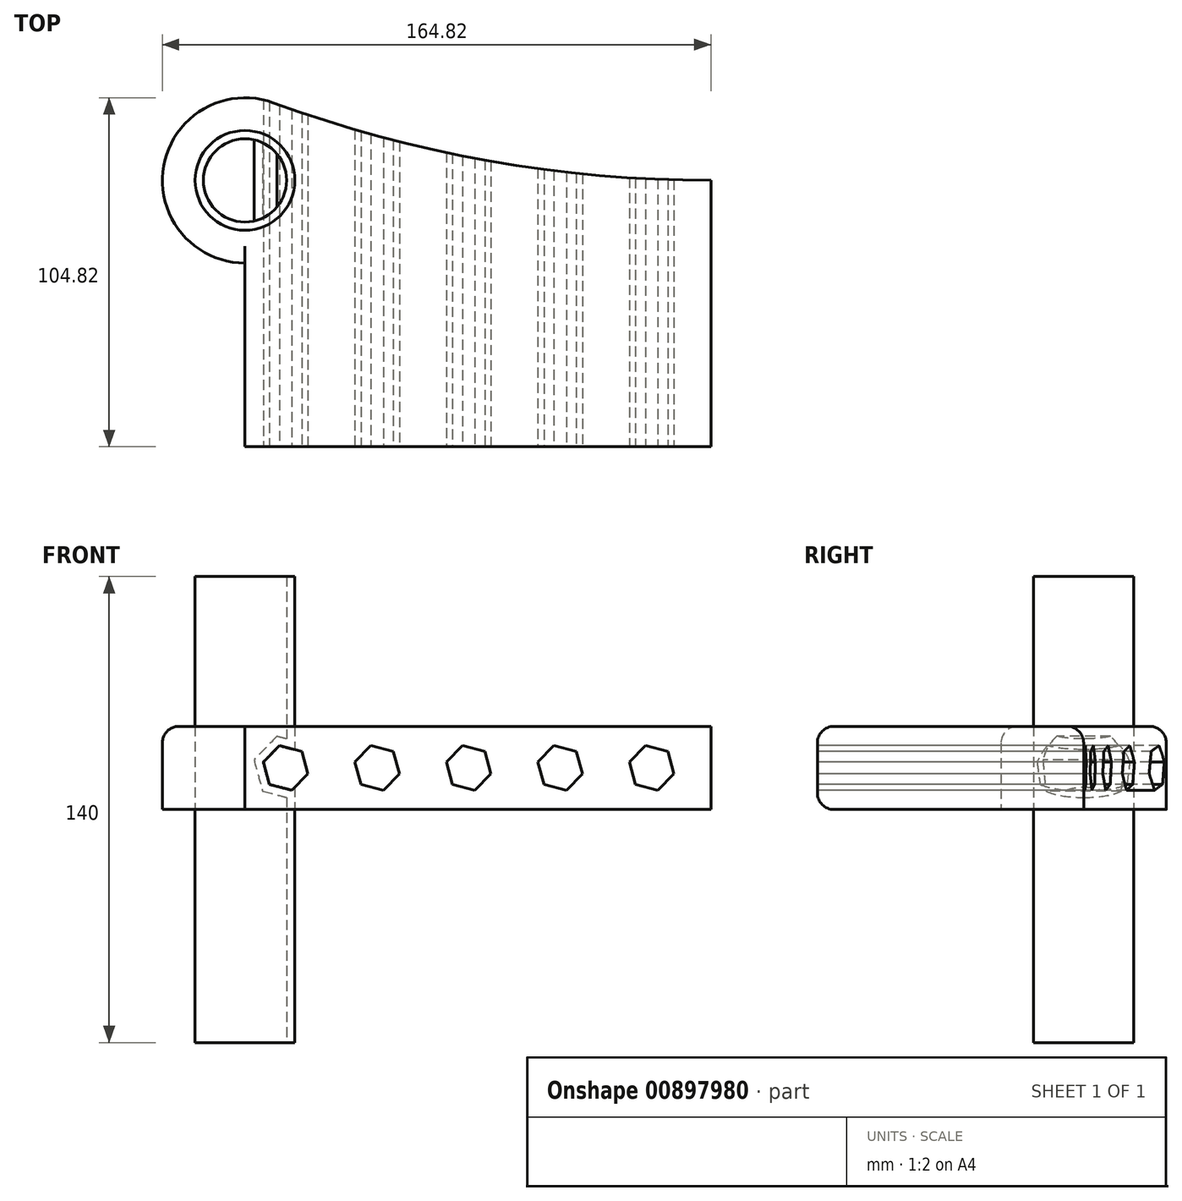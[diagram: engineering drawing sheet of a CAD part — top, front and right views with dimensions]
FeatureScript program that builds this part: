
annotation { "Feature Type Name" : "Feature", "Feature Type Description" : "" }
export const myFeature = defineFeature(function(context is Context, id is Id, definition is map)
    precondition{}
    {
        {
            var Q0;
            Q0=qCreatedBy(makeId("Top.planeOp"),FACE);
            var sketch = newSketch(context, id + "F0", { "sketchPlane" : qUnion([Q0])});
            skLineSegment(sketch, "E0.bottom", {"start": v(70, -40) * mm, "end": v(-70, -40) * mm});
            skLineSegment(sketch, "E0.top", {"start": v(70, 40) * mm, "end": v(-70, 40) * mm});
            skLineSegment(sketch, "E0.left", {"start": v(70, -40) * mm, "end": v(70, 40) * mm});
            skLineSegment(sketch, "E0.right", {"start": v(-70, -40) * mm, "end": v(-70, 40) * mm});
            skPoint(sketch, "E0.middle", {"position": v(0, 0) * mm});
            skCircle(sketch, "E1", {"center": v(-70, 40) * mm, "radius": 24.82 * mm});
            skArc(sketch, "E2", {"start": v(-61.47, 63.3) * mm, "mid": v(3.24, 45.87) * mm, "end": v(70, 40) * mm});
            skCircle(sketch, "E3", {"center": v(-70, 40) * mm, "radius": 15 * mm});
            skSolve(sketch);
        }
        {
            var Q0;
            {var subQ5=sQuery(id+"F0.wireOp",EDGE,"E0.bottom");Q0=makeQuery(id+"F0.imprint","IMPRINT",FACE,{"disambiguationData":[TD([[makeQuery(id+"F0.imprint","IMPRINT",EDGE,{"derivedFrom":subQ5}),-1.0]])]});}
            var Q1;
            {var subQ0=sQuery(id+"F0.wireOp",EDGE,"E1");var subQ4=sQuery(id+"F0.wireOp",EDGE,"E0.top");var subQ5=makeQuery(id+"F0.imprint","INTERSECT",VERTEX,{"derivedFrom":[subQ4,subQ0]});Q1=makeQuery(id+"F0.imprint","IMPRINT",FACE,{"disambiguationData":[TD([[makeQuery(id+"F0.imprint","IMPRINT",EDGE,{"disambiguationData":[TD([[subQ5,-1.0]])],"derivedFrom":subQ4}),-1.0]])]});}
            var Q2;
            {var subQ0=sQuery(id+"F0.wireOp",EDGE,"E2");Q2=makeQuery(id+"F0.imprint","IMPRINT",FACE,{"disambiguationData":[TD([[makeQuery(id+"F0.imprint","IMPRINT",EDGE,{"derivedFrom":subQ0}),-1.0]])]});}
            var Q3;
            {var subQ0=sQuery(id+"F0.wireOp",EDGE,"E1");var subQ1=sQuery(id+"F0.wireOp",EDGE,"E0.top");var subQ2=makeQuery(id+"F0.imprint","INTERSECT",VERTEX,{"derivedFrom":[subQ1,subQ0]});Q3=makeQuery(id+"F0.imprint","IMPRINT",FACE,{"disambiguationData":[TD([[makeQuery(id+"F0.imprint","IMPRINT",EDGE,{"disambiguationData":[TD([[subQ2,-1.0]])],"derivedFrom":subQ1}),1.0]])]});}
            extrude(context, id + "F1", {"entities" : qUnion([Q0, Q1, Q2, Q3]), "depth" : 25 * mm, "offsetDistance" : 25 * mm});
        }
        {
            var Q0;
            {var subQ0=sQuery(id+"F0.wireOp",EDGE,"E0.right");var subQ1=sQuery(id+"F0.wireOp",EDGE,"E0.top");var subQ2=makeQuery(id+"F0.imprint","INTERSECT",VERTEX,{"derivedFrom":[subQ1,subQ0]});Q0=makeQuery(id+"F0.imprint","IMPRINT",FACE,{"disambiguationData":[TD([[makeQuery(id+"F0.imprint","IMPRINT",EDGE,{"disambiguationData":[TD([[subQ2,1.0]])],"derivedFrom":subQ1}),-1.0]])]});}
            var Q1;
            {var subQ0=sQuery(id+"F0.wireOp",EDGE,"E0.right");var subQ1=sQuery(id+"F0.wireOp",EDGE,"E0.top");var subQ2=makeQuery(id+"F0.imprint","INTERSECT",VERTEX,{"derivedFrom":[subQ1,subQ0]});Q1=makeQuery(id+"F0.imprint","IMPRINT",FACE,{"disambiguationData":[TD([[makeQuery(id+"F0.imprint","IMPRINT",EDGE,{"disambiguationData":[TD([[subQ2,1.0]])],"derivedFrom":subQ1}),1.0]])]});}
            extrude(context, id + "F2", {"entities" : qUnion([Q0, Q1]), "endBound" : BoundingType.SYMMETRIC, "depth" : 140 * mm, "offsetDistance" : 25 * mm});
        }
        {
            var Q0;
            Q0=makeQuery(id+"F1.opExtrude","SWEPT_FACE",FACE,{"disambiguationData":[OSD([sQuery(id+"F0.wireOp",EDGE,"E0.bottom")])]});
            var sketch = newSketch(context, id + "F3", { "sketchPlane" : qUnion([Q0])});
            skCircle(sketch, "E4.cCircle", {"center": v(-57.79, 12.5) * mm, "radius": 6 * mm, "construction": true});
            skPoint(sketch, "E4.cCircle.centerSnap0", {"position": v(-70, 12.5) * mm});
            skLineSegment(sketch, "E4.0", {"start": v(-51.07, 10.76) * mm, "end": v(-55.93, 5.81) * mm});
            skLineSegment(sketch, "E4.1", {"start": v(-55.93, 5.81) * mm, "end": v(-62.65, 7.55) * mm});
            skLineSegment(sketch, "E4.2", {"start": v(-62.65, 7.55) * mm, "end": v(-64.5, 14.24) * mm});
            skLineSegment(sketch, "E4.3", {"start": v(-64.5, 14.24) * mm, "end": v(-59.65, 19.19) * mm});
            skLineSegment(sketch, "E4.4", {"start": v(-59.65, 19.19) * mm, "end": v(-52.93, 17.45) * mm});
            skLineSegment(sketch, "E4.5", {"start": v(-52.93, 17.45) * mm, "end": v(-51.07, 10.76) * mm});
            skPoint(sketch, "E4.0.midPoint", {"position": v(-53.5, 8.29) * mm});
            skLineSegment(sketch, "E5.1.0.0", {"start": v(-35.15, 7.55) * mm, "end": v(-37, 14.24) * mm});
            skLineSegment(sketch, "E5.1.0.1", {"start": v(-37, 14.24) * mm, "end": v(-32.15, 19.19) * mm});
            skLineSegment(sketch, "E5.1.0.2", {"start": v(-32.15, 19.19) * mm, "end": v(-25.43, 17.45) * mm});
            skLineSegment(sketch, "E5.1.0.3", {"start": v(-25.43, 17.45) * mm, "end": v(-23.57, 10.76) * mm});
            skLineSegment(sketch, "E5.1.0.4", {"start": v(-23.57, 10.76) * mm, "end": v(-28.43, 5.81) * mm});
            skLineSegment(sketch, "E5.1.0.5", {"start": v(-28.43, 5.81) * mm, "end": v(-35.15, 7.55) * mm});
            skLineSegment(sketch, "E5.2.0.0", {"start": v(-7.65, 7.55) * mm, "end": v(-9.5, 14.24) * mm});
            skLineSegment(sketch, "E5.2.0.1", {"start": v(-9.5, 14.24) * mm, "end": v(-4.65, 19.19) * mm});
            skLineSegment(sketch, "E5.2.0.2", {"start": v(-4.65, 19.19) * mm, "end": v(2.07, 17.45) * mm});
            skLineSegment(sketch, "E5.2.0.3", {"start": v(2.07, 17.45) * mm, "end": v(3.93, 10.76) * mm});
            skLineSegment(sketch, "E5.2.0.4", {"start": v(3.93, 10.76) * mm, "end": v(-0.93, 5.81) * mm});
            skLineSegment(sketch, "E5.2.0.5", {"start": v(-0.93, 5.81) * mm, "end": v(-7.65, 7.55) * mm});
            skLineSegment(sketch, "E5.3.0.0", {"start": v(19.85, 7.55) * mm, "end": v(18, 14.24) * mm});
            skLineSegment(sketch, "E5.3.0.1", {"start": v(18, 14.24) * mm, "end": v(22.85, 19.19) * mm});
            skLineSegment(sketch, "E5.3.0.2", {"start": v(22.85, 19.19) * mm, "end": v(29.57, 17.45) * mm});
            skLineSegment(sketch, "E5.3.0.3", {"start": v(29.57, 17.45) * mm, "end": v(31.43, 10.76) * mm});
            skLineSegment(sketch, "E5.3.0.4", {"start": v(31.43, 10.76) * mm, "end": v(26.57, 5.81) * mm});
            skLineSegment(sketch, "E5.3.0.5", {"start": v(26.57, 5.81) * mm, "end": v(19.85, 7.55) * mm});
            skLineSegment(sketch, "E5.4.0.0", {"start": v(47.35, 7.55) * mm, "end": v(45.5, 14.24) * mm});
            skLineSegment(sketch, "E5.4.0.1", {"start": v(45.5, 14.24) * mm, "end": v(50.35, 19.19) * mm});
            skLineSegment(sketch, "E5.4.0.2", {"start": v(50.35, 19.19) * mm, "end": v(57.07, 17.45) * mm});
            skLineSegment(sketch, "E5.4.0.3", {"start": v(57.07, 17.45) * mm, "end": v(58.93, 10.76) * mm});
            skLineSegment(sketch, "E5.4.0.4", {"start": v(58.93, 10.76) * mm, "end": v(54.07, 5.81) * mm});
            skLineSegment(sketch, "E5.4.0.5", {"start": v(54.07, 5.81) * mm, "end": v(47.35, 7.55) * mm});
            skLineSegment(sketch, "E5.direction1", {"start": v(-62.65, 7.55) * mm, "end": v(-35.15, 7.55) * mm, "construction": true});
            skSolve(sketch);
        }
        {
            var Q0;
            Q0=makeQuery(id+"F3.imprint","IMPRINT",FACE,{"disambiguationData":[TD([[makeQuery(id+"F3.imprint","IMPRINT",EDGE,{"derivedFrom":sQuery(id+"F3.wireOp",EDGE,"E4.0")}),-1.0]])]});
            var Q1;
            Q1=makeQuery(id+"F3.imprint","IMPRINT",FACE,{"disambiguationData":[TD([[makeQuery(id+"F3.imprint","IMPRINT",EDGE,{"derivedFrom":sQuery(id+"F3.wireOp",EDGE,"E5.1.0.0")}),-1.0]])]});
            var Q2;
            Q2=makeQuery(id+"F3.imprint","IMPRINT",FACE,{"disambiguationData":[TD([[makeQuery(id+"F3.imprint","IMPRINT",EDGE,{"derivedFrom":sQuery(id+"F3.wireOp",EDGE,"E5.2.0.0")}),-1.0]])]});
            var Q3;
            Q3=makeQuery(id+"F3.imprint","IMPRINT",FACE,{"disambiguationData":[TD([[makeQuery(id+"F3.imprint","IMPRINT",EDGE,{"derivedFrom":sQuery(id+"F3.wireOp",EDGE,"E5.3.0.0")}),-1.0]])]});
            var Q4;
            Q4=makeQuery(id+"F3.imprint","IMPRINT",FACE,{"disambiguationData":[TD([[makeQuery(id+"F3.imprint","IMPRINT",EDGE,{"derivedFrom":sQuery(id+"F3.wireOp",EDGE,"E5.4.0.0")}),-1.0]])]});
            extrude(context, id + "F4", {"entities" : qUnion([Q0, Q1, Q2, Q3, Q4]), "operationType" : NewBodyOperationType.REMOVE, "oppositeDirection" : true, "depth" : 120 * mm, "offsetDistance" : 25 * mm});
        }
        {
            var Q0;
            Q0=makeQuery(id+"F1.opExtrude","CAP_EDGE",EDGE,{"disambiguationData":[OSD([sQuery(id+"F0.wireOp",EDGE,"E0.bottom")])],"isStart":false});
            var Q1;
            Q1=makeQuery(id+"F1.opExtrude","CAP_EDGE",EDGE,{"disambiguationData":[OSD([sQuery(id+"F0.wireOp",EDGE,"E0.bottom")])],"isStart":true});
            var Q2;
            Q2=makeQuery(id+"F1.opExtrude","CAP_EDGE",EDGE,{"disambiguationData":[OSD([sQuery(id+"F0.wireOp",EDGE,"E2")])],"isStart":false});
            fillet(context, id + "F5", {"entities" : qUnion([Q0, Q1, Q2]), "radius" : 5 * mm, "tangentPropagation" : true, "allowEdgeOverflow" : false});
        }
        {
            var Q0;
            Q0=makeQuery(id+"F2.opExtrude","CAP_FACE",FACE,{"disambiguationData":[OSD([sQuery(id+"F0.wireOp",EDGE,"E3")])],"isStart":false});
            var Q1;
            Q1=makeQuery(id+"F2.opExtrude","CAP_FACE",FACE,{"disambiguationData":[OSD([sQuery(id+"F0.wireOp",EDGE,"E3")])],"isStart":true});
            shell(context, id + "F6", {"entities" : qUnion([Q0, Q1]), "thickness" : 2.5 * mm});
        }
    });
